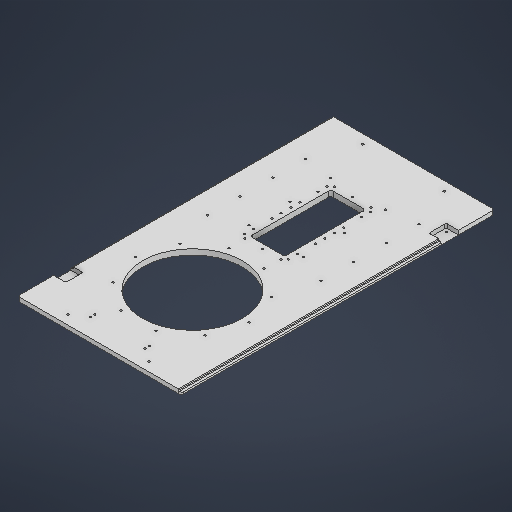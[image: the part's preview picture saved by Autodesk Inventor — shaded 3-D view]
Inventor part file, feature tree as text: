
AUTODESK INVENTOR PART (.ipt)
format: ipt  version: 2025 (Build 290162000, 162)  size: 482,304 bytes
history: native  units: in
note: dims shown in document units (in); Inventor stores cm internally (conversion verified against a paired STEP export)
features: sketch x16, extrude x5, hole x5, chamfer x4, fillet x3, plane x2
ambient origin geometry x8: Origin, YZ Plane, XZ Plane, XY Plane, X Axis, Y Axis, Z Axis, Center Point
bodies: Solid1 (feature_tree)
feature tree (35):
  extrude  "Extrusion1"  Depth=27.1654in
  sketch  "Sketch2"  dims[d5=8.6614in d6=0.0in d7=0.0in]
  extrude  "Extrusion2"  Depth=0.4724in
  plane  "Work Plane1"
  hole  "Hole3"  [1 undecoded]
  sketch  "Sketch7"  dims[d82=1.063in]
  plane  "Work Plane2"
  hole  "Hole4"  [1 undecoded]
  sketch  "Sketch9"  dims[d84=1.4961in]
  fillet  "Fillet2"  Radius=7.0625in
  extrude  "Extrusion7"  Depth=0.3937in
  extrude  "Extrusion8"  Depth=9.8425in
  chamfer  "Chamfer3"  Distance=3.937in Angle=360.0deg
  chamfer  "Chamfer4"  Distance=0.1181in
  hole  "Hole5"  [1 undecoded]
  chamfer  "Chamfer5"  Distance=0.3543in
  hole  "Hole6"  [1 undecoded]
  sketch  "Sketch15"  dims[d88=0.1969in d95=0.1181in d96=0.1181in d97=0.3543in d98=0.0in d99=0.2362in d100=0.2362in d101=0.122in d102=0.0in d103=0.0787in d104=0.1378in d105=45.0deg d106=0.0787in d107=0.1378in d108=45.0deg d110=0.315in d111=0.8661in d113=0.1299in d114=0.1299in d115=0.1299in d116=0.1299in d118=0.315in d119=0.8661in d122=0.1276in d123=0.315in d124=0.1575in d125=0.0787in d126=90.0deg d127=0.315in d128=0.8108in d129=0.0138in d130=0.0787in d131=45.0deg d146=3.9469in d147=0.7874in d148=0.3937in d149=0.1575in d150=3.937in d152=1.1811in d153=0.3937in d155=0.3937in d157=0.1575in d158=1.1811in d160=0.7874in d161=0.3937in d163=0.3937in d165=9.8425in d166=0.1575in d167=2.9528in d168=1.1811in d169=3.1496in d171=1.4173in d172=0.3937in d174=0.3937in d176=0.1628in d177=0.3937in d178=0.1575in d179=0.0787in d180=90.0deg d181=0.3937in d182=0.8108in d191=3.0in d192=7.0in d193=6.4961in d194=0.8312in d195=0.0in d196=0.1969in d197=0.3937in d198=0.1969in d199=1.9685in d201=0.7874in d202=0.3937in d204=0.3937in d206=0.3189in d207=0.1969in d208=0.3189in d209=1.9685in d211=0.7874in d212=0.3937in d214=0.3937in d216=0.1628in d217=0.3937in d218=0.1575in d219=0.0787in d220=90.0deg d221=0.3937in d222=0.8108in d232=0.1969in d233=0.1181in d234=0.0787in d235=45.0deg d236=0.1575in d237=0.1575in d26=0.0394in d27=0.0394in d28=0.0394in d29=0.0059in d30=0.0098in d31=0.0148in d32=0.5635in d33=0.0295in d34=0.8108in d35=0.0025in d36=0.0295in d37=0.0148in d66=0.0197in d67=0.0344in d230=0.0197in d231=0.0344in]
  extrude  "Extrusion11"  Depth=0.2362in
  fillet  "Fillet3"  Radius=0.122in
  hole  "Hole7"  [1 undecoded]
  fillet  "Fillet5"  Radius=0.1378in
  chamfer  "Chamfer6"  Distance=0.315in
  sketch  "Sketch1"  dims[d0=14.1732in d1=27.1654in]
  sketch  "Sketch6"  dims[d74=0.1628in d75=0.3937in d76=0.1575in d77=0.0787in d78=90.0deg d79=0.3937in d80=0.8108in]
  sketch  "Sketch8"  dims[d83=1.063in]
  sketch  "Sketch Circular Pattern4"  dims[d57=0.1936in d58=0.3937in d59=0.1575in d60=0.0787in d61=90.0deg d62=0.3937in d63=0.8108in d64=10.3543in]
  sketch  "Sketch10"  dims[d85=1.4961in]
  sketch  "Sketch11"  dims[d86=3.1102in]
  sketch  "Sketch12"  dims[d87=3.1102in]
  sketch  "Sketch Rectangular Pattern1"  dims[d2=0.4724in d3=0.0in d4=8.0709in]
  sketch  "Sketch Rectangular Pattern2"  dims[d8=10.6299in d50=5.9055in d55=7.0625in]
  sketch  "Sketch Rectangular Pattern3"  dims[d56=25.5906in]
  sketch  "Sketch Rectangular Pattern4"  dims[d65=10.6299in d68=9.8425in]
  sketch  "Sketch Rectangular Pattern5"  dims[d69=0.1575in d70=3.937in d72=360.0deg]
note: 5 required parameter values undecoded (feature->parameter linkage not recoverable at this tier; creation-order binding heuristic only, values carry confidence <= 0.55)
